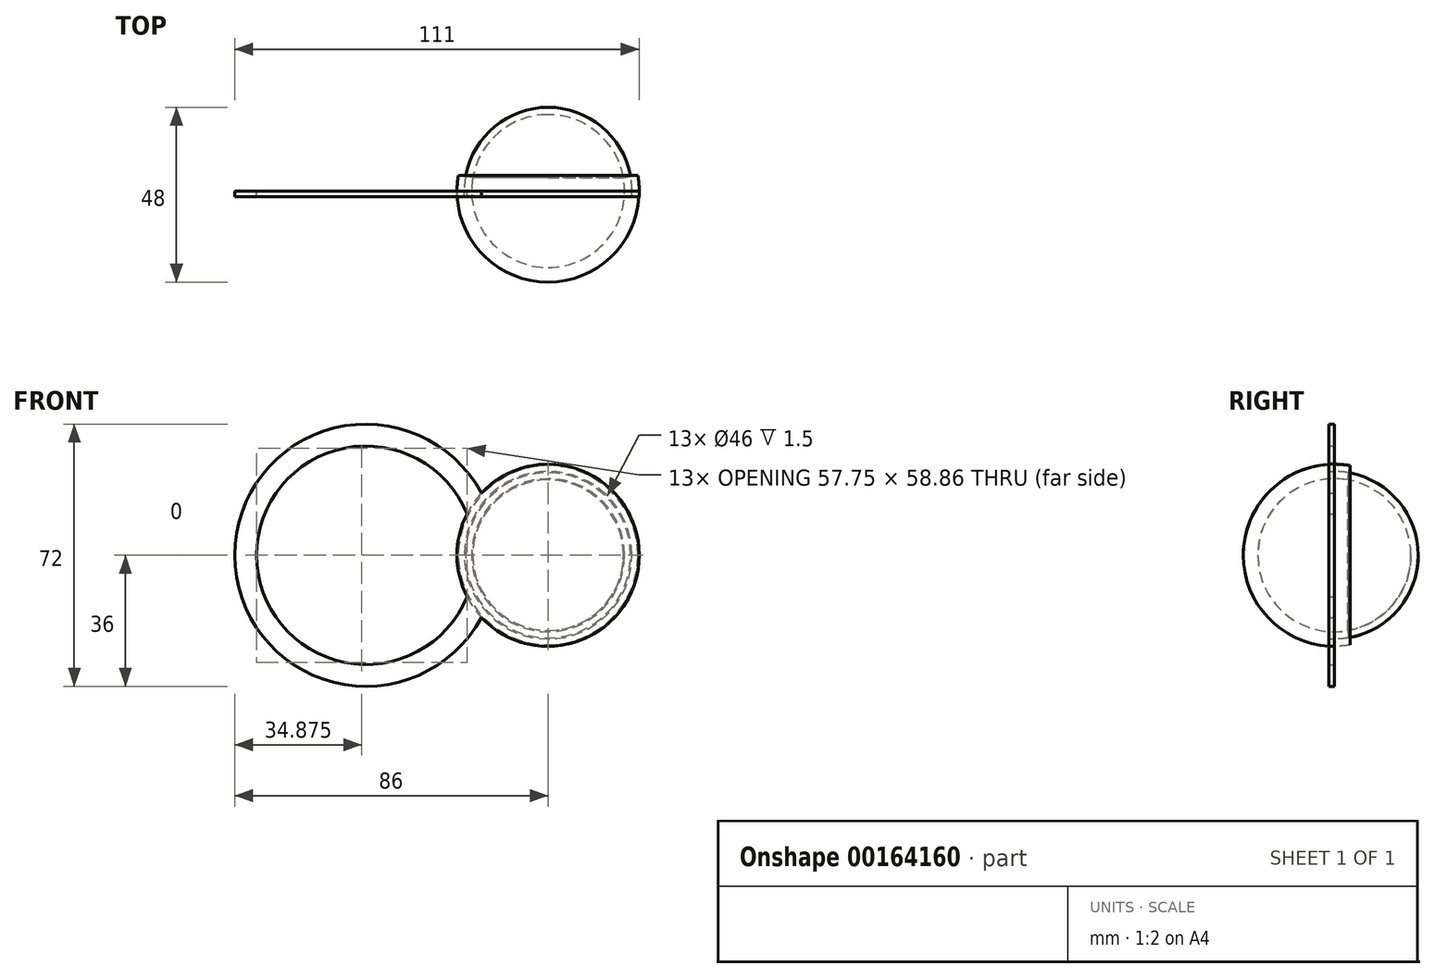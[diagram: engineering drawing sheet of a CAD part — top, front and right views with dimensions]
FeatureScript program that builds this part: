
annotation { "Feature Type Name" : "Feature", "Feature Type Description" : "" }
export const myFeature = defineFeature(function(context is Context, id is Id, definition is map)
    precondition{}
    {
        {
            var Q0;
            Q0=qCreatedBy(makeId("Right.planeOp"),FACE);
            var sketch = newSketch(context, id + "F0", { "sketchPlane" : qUnion([Q0])});
            skCircle(sketch, "E0", {"center": v(0, 0) * mm, "radius": 25 * mm});
            skCircle(sketch, "E1", {"center": v(0, 0) * mm, "radius": 23 * mm});
            skLineSegment(sketch, "E2", {"start": v(0, 25) * mm, "end": v(0, -25) * mm});
            skCircle(sketch, "E3", {"center": v(0, 0) * mm, "radius": 21 * mm});
            skLineSegment(sketch, "E4", {"start": v(-4, 22.65) * mm, "end": v(4.34, -24.62) * mm});
            skLineSegment(sketch, "E5", {"start": v(-25, 0) * mm, "end": v(25, 0) * mm});
            skSolve(sketch);
        }
        {
            var Q0;
            Q0=qCreatedBy(makeId("Front.planeOp"),FACE);
            var sketch = newSketch(context, id + "F1", { "sketchPlane" : qUnion([Q0])});
            skLineSegment(sketch, "E6.0", {"start": v(0, 25) * mm, "end": v(0, -25) * mm});
            skCircle(sketch, "E7", {"center": v(0, 0) * mm, "radius": 25 * mm});
            skLineSegment(sketch, "E8.0", {"start": v(0, 23) * mm, "end": v(0, -23) * mm});
            skCircle(sketch, "E9", {"center": v(0, 0) * mm, "radius": 23 * mm});
            skLineSegment(sketch, "E10", {"start": v(0, 0) * mm, "end": v(80, 0) * mm});
            skFitSpline(sketch, "E11", {"points": [v(80, 0) * mm, v(65.88, 17.16) * mm, v(0, 25) * mm], "startDerivative": vector(-4.2, 59.99) * mm, "endDerivative": vector(-140.9, -3.11) * mm});
            skFitSpline(sketch, "E12", {"points": [v(72, 0) * mm, v(58.74, 13.75) * mm, v(0, 23) * mm], "startDerivative": vector(-12.5, 61.65) * mm, "endDerivative": vector(-113.4, 12.13) * mm});
            skFitSpline(sketch, "E13.MirrorCS", {"points": [v(72, 0) * mm, v(58.74, -13.75) * mm, v(0, -23) * mm], "startDerivative": vector(-12.5, -61.65) * mm, "endDerivative": vector(-113.4, -12.13) * mm});
            skFitSpline(sketch, "E14.MirrorCS", {"points": [v(80, 0) * mm, v(65.88, -17.16) * mm, v(0, -25) * mm], "startDerivative": vector(-4.2, -59.99) * mm, "endDerivative": vector(-140.9, 3.11) * mm});
            skFitSpline(sketch, "E15.MirrorCS", {"points": [v(-80, 0) * mm, v(-65.88, 17.16) * mm, v(0, 25) * mm], "startDerivative": vector(4.2, 59.99) * mm, "endDerivative": vector(140.9, -3.11) * mm});
            skFitSpline(sketch, "E16.MirrorCS", {"points": [v(-72, 0) * mm, v(-58.74, 13.75) * mm, v(0, 23) * mm], "startDerivative": vector(12.5, 61.65) * mm, "endDerivative": vector(113.4, 12.13) * mm});
            skFitSpline(sketch, "E17.MirrorCS", {"points": [v(-72, 0) * mm, v(-58.74, -13.75) * mm, v(0, -23) * mm], "startDerivative": vector(12.5, -61.65) * mm, "endDerivative": vector(113.4, -12.13) * mm});
            skFitSpline(sketch, "E18.MirrorCS", {"points": [v(-80, 0) * mm, v(-65.88, -17.16) * mm, v(0, -25) * mm], "startDerivative": vector(4.2, -59.99) * mm, "endDerivative": vector(140.9, 3.11) * mm});
            skSolve(sketch);
        }
        {
            var Q0;
            Q0=qCreatedBy(makeId("Front.planeOp"),FACE);
            var sketch = newSketch(context, id + "F2", { "sketchPlane" : qUnion([Q0])});
            skCircle(sketch, "E19.0", {"center": v(0, 0) * mm, "radius": 25 * mm});
            skCircle(sketch, "E20.0", {"center": v(0, 0) * mm, "radius": 23 * mm});
            skCircle(sketch, "E21", {"center": v(-50, 0) * mm, "radius": 36 * mm});
            skCircle(sketch, "E22", {"center": v(-50, 0) * mm, "radius": 30 * mm});
            skSolve(sketch);
        }
        {
            var Q0;
            {var subQ0=sQuery(id+"F2.wireOp",EDGE,"E21");var subQ1=sQuery(id+"F2.wireOp",EDGE,"E19.0");var subQ2=makeQuery(id+"F2.imprint","INTERSECT",VERTEX,{"disambiguationData":[OD(0.0)],"derivedFrom":[subQ1,subQ0]});Q0=makeQuery(id+"F2.imprint","IMPRINT",FACE,{"disambiguationData":[TD([[makeQuery(id+"F2.imprint","IMPRINT",EDGE,{"disambiguationData":[TD([[subQ2,-1.0]])],"derivedFrom":subQ1}),-1.0]])]});}
            var Q1;
            {var subQ0=sQuery(id+"F2.wireOp",EDGE,"E21");var subQ1=sQuery(id+"F2.wireOp",EDGE,"E19.0");var subQ2=makeQuery(id+"F2.imprint","INTERSECT",VERTEX,{"disambiguationData":[OD(0.0)],"derivedFrom":[subQ1,subQ0]});Q1=makeQuery(id+"F2.imprint","IMPRINT",FACE,{"disambiguationData":[TD([[makeQuery(id+"F2.imprint","IMPRINT",EDGE,{"disambiguationData":[TD([[subQ2,-1.0]])],"derivedFrom":subQ1}),1.0]])]});}
            var Q2;
            {var subQ0=sQuery(id+"F2.wireOp",EDGE,"E21");var subQ1=sQuery(id+"F2.wireOp",EDGE,"E19.0");var subQ2=makeQuery(id+"F2.imprint","INTERSECT",VERTEX,{"disambiguationData":[OD(1.0)],"derivedFrom":[subQ1,subQ0]});Q2=makeQuery(id+"F2.imprint","IMPRINT",FACE,{"disambiguationData":[TD([[makeQuery(id+"F2.imprint","IMPRINT",EDGE,{"disambiguationData":[TD([[subQ2,1.0]])],"derivedFrom":subQ1}),1.0]])]});}
            var Q3;
            {var subQ0=sQuery(id+"F2.wireOp",EDGE,"E22");var subQ1=sQuery(id+"F2.wireOp",EDGE,"E19.0");var subQ2=makeQuery(id+"F2.imprint","INTERSECT",VERTEX,{"disambiguationData":[OD(0.0)],"derivedFrom":[subQ1,subQ0]});Q3=makeQuery(id+"F2.imprint","IMPRINT",FACE,{"disambiguationData":[TD([[makeQuery(id+"F2.imprint","IMPRINT",EDGE,{"disambiguationData":[TD([[subQ2,-1.0]])],"derivedFrom":subQ1}),1.0]])]});}
            var Q4;
            {var subQ0=sQuery(id+"F2.wireOp",EDGE,"E21");var subQ1=sQuery(id+"F2.wireOp",EDGE,"E19.0");var subQ2=makeQuery(id+"F2.imprint","INTERSECT",VERTEX,{"disambiguationData":[OD(0.0)],"derivedFrom":[subQ1,subQ0]});Q4=makeQuery(id+"F2.imprint","IMPRINT",FACE,{"disambiguationData":[TD([[makeQuery(id+"F2.imprint","IMPRINT",EDGE,{"disambiguationData":[TD([[subQ2,1.0]])],"derivedFrom":subQ1}),1.0]])]});}
            extrude(context, id + "F3", {"entities" : qUnion([Q0, Q1, Q2, Q3, Q4]), "depth" : 1.5 * mm});
        }
        {
            var Q0;
            {var subQ0=sQuery(id+"F0.wireOp",EDGE,"E2");var subQ1=sQuery(id+"F0.wireOp",EDGE,"E0");var subQ2=makeQuery(id+"F0.imprint","INTERSECT",VERTEX,{"disambiguationData":[OD(0.0)],"derivedFrom":[subQ1,subQ0]});Q0=makeQuery(id+"F0.imprint","IMPRINT",FACE,{"disambiguationData":[TD([[makeQuery(id+"F0.imprint","IMPRINT",EDGE,{"disambiguationData":[TD([[subQ2,-1.0]])],"derivedFrom":subQ1}),1.0]])]});}
            var Q1;
            {var subQ0=sQuery(id+"F0.wireOp",EDGE,"E4");var subQ1=sQuery(id+"F0.wireOp",EDGE,"E1");var subQ2=makeQuery(id+"F0.imprint","INTERSECT",VERTEX,{"disambiguationData":[OD(0.0)],"derivedFrom":[subQ1,subQ0]});Q1=makeQuery(id+"F0.imprint","IMPRINT",FACE,{"disambiguationData":[TD([[makeQuery(id+"F0.imprint","IMPRINT",EDGE,{"disambiguationData":[TD([[subQ2,-1.0]])],"derivedFrom":subQ1}),1.0]])]});}
            var Q2;
            Q2=sQuery(id+"F0.wireOp",EDGE,"E5");
            revolve(context, id + "F4", {"entities" : qUnion([Q0, Q1]), "axis" : qUnion([Q2]), "revolveType" : RevolveType.FULL});
        }
        {
            var Q0;
            {var subQ0=sQuery(id+"F0.wireOp",EDGE,"E4");var subQ1=sQuery(id+"F0.wireOp",EDGE,"E1");var subQ2=makeQuery(id+"F0.imprint","INTERSECT",VERTEX,{"disambiguationData":[OD(0.0)],"derivedFrom":[subQ1,subQ0]});Q0=makeQuery(id+"F0.imprint","IMPRINT",FACE,{"disambiguationData":[TD([[makeQuery(id+"F0.imprint","IMPRINT",EDGE,{"disambiguationData":[TD([[subQ2,1.0]])],"derivedFrom":subQ1}),1.0]])]});}
            var Q1;
            {var subQ0=sQuery(id+"F0.wireOp",EDGE,"E2");var subQ1=sQuery(id+"F0.wireOp",EDGE,"E1");var subQ2=makeQuery(id+"F0.imprint","INTERSECT",VERTEX,{"disambiguationData":[OD(0.0)],"derivedFrom":[subQ1,subQ0]});Q1=makeQuery(id+"F0.imprint","IMPRINT",FACE,{"disambiguationData":[TD([[makeQuery(id+"F0.imprint","IMPRINT",EDGE,{"disambiguationData":[TD([[subQ2,1.0]])],"derivedFrom":subQ1}),1.0]])]});}
            var Q2;
            {var subQ0=sQuery(id+"F0.wireOp",EDGE,"E2");var subQ1=sQuery(id+"F0.wireOp",EDGE,"E0");var subQ2=makeQuery(id+"F0.imprint","INTERSECT",VERTEX,{"disambiguationData":[OD(0.0)],"derivedFrom":[subQ1,subQ0]});Q2=makeQuery(id+"F0.imprint","IMPRINT",FACE,{"disambiguationData":[TD([[makeQuery(id+"F0.imprint","IMPRINT",EDGE,{"disambiguationData":[TD([[subQ2,1.0]])],"derivedFrom":subQ1}),1.0]])]});}
            var Q3;
            Q3=sQuery(id+"F0.wireOp",EDGE,"E5");
            revolve(context, id + "F5", {"entities" : qUnion([Q0, Q1, Q2]), "axis" : qUnion([Q3]), "revolveType" : RevolveType.FULL});
        }
    });
